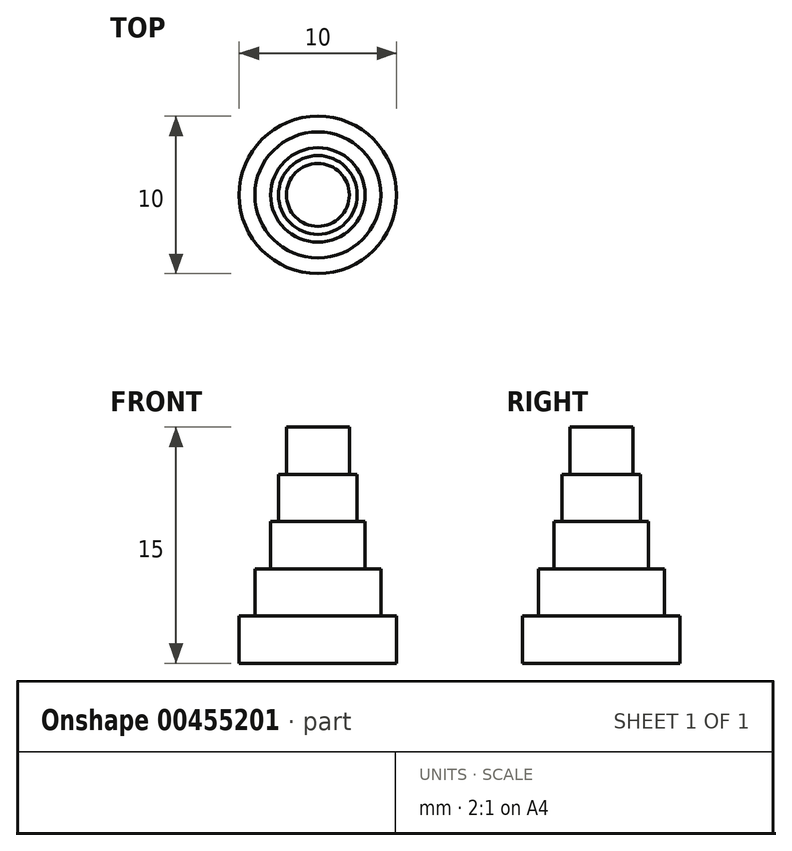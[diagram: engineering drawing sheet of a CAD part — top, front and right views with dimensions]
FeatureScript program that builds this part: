
annotation { "Feature Type Name" : "Feature", "Feature Type Description" : "" }
export const myFeature = defineFeature(function(context is Context, id is Id, definition is map)
    precondition{}
    {
        {
            var Q0;
            Q0=qCreatedBy(makeId("Top.planeOp"),FACE);
            var sketch = newSketch(context, id + "F0", { "sketchPlane" : qUnion([Q0])});
            skCircle(sketch, "E0", {"center": v(0, 0) * mm, "radius": 5 * mm});
            skSolve(sketch);
        }
        {
            var Q0;
            Q0=makeQuery(id+"F0.imprint","IMPRINT",FACE,{"disambiguationData":[TD([[makeQuery(id+"F0.imprint","IMPRINT",EDGE,{"derivedFrom":sQuery(id+"F0.wireOp",EDGE,"E0")}),1.0]])]});
            extrude(context, id + "F1", {"entities" : qUnion([Q0]), "depth" : 3 * mm});
        }
        {
            var Q0;
            Q0=makeQuery(id+"F1.opExtrude","CAP_FACE",FACE,{"disambiguationData":[OSD([sQuery(id+"F0.wireOp",EDGE,"E0")])],"isStart":false});
            var sketch = newSketch(context, id + "F2", { "sketchPlane" : qUnion([Q0])});
            skCircle(sketch, "E1", {"center": v(0, 0) * mm, "radius": 4 * mm});
            skSolve(sketch);
        }
        {
            var Q0;
            Q0=makeQuery(id+"F2.imprint","IMPRINT",FACE,{"disambiguationData":[TD([[makeQuery(id+"F2.imprint","IMPRINT",EDGE,{"derivedFrom":sQuery(id+"F2.wireOp",EDGE,"E1")}),1.0]])]});
            extrude(context, id + "F3", {"entities" : qUnion([Q0]), "operationType" : NewBodyOperationType.ADD, "depth" : 3 * mm});
        }
        {
            var Q0;
            Q0=makeQuery(id+"F3.opExtrude","CAP_FACE",FACE,{"disambiguationData":[OSD([sQuery(id+"F2.wireOp",EDGE,"E1")])],"isStart":false});
            var sketch = newSketch(context, id + "F4", { "sketchPlane" : qUnion([Q0])});
            skCircle(sketch, "E2", {"center": v(0, 0) * mm, "radius": 3 * mm});
            skSolve(sketch);
        }
        {
            var Q0;
            Q0=makeQuery(id+"F4.imprint","IMPRINT",FACE,{"disambiguationData":[TD([[makeQuery(id+"F4.imprint","IMPRINT",EDGE,{"derivedFrom":sQuery(id+"F4.wireOp",EDGE,"E2")}),1.0]])]});
            extrude(context, id + "F5", {"entities" : qUnion([Q0]), "operationType" : NewBodyOperationType.ADD, "depth" : 3 * mm});
        }
        {
            var Q0;
            Q0=makeQuery(id+"F5.opExtrude","CAP_FACE",FACE,{"disambiguationData":[OSD([sQuery(id+"F4.wireOp",EDGE,"E2")])],"isStart":false});
            var sketch = newSketch(context, id + "F6", { "sketchPlane" : qUnion([Q0])});
            skCircle(sketch, "E3", {"center": v(0, 0) * mm, "radius": 2.5 * mm});
            skSolve(sketch);
        }
        {
            var Q0;
            Q0=makeQuery(id+"F6.imprint","IMPRINT",FACE,{"disambiguationData":[TD([[makeQuery(id+"F6.imprint","IMPRINT",EDGE,{"derivedFrom":sQuery(id+"F6.wireOp",EDGE,"E3")}),1.0]])]});
            extrude(context, id + "F7", {"entities" : qUnion([Q0]), "operationType" : NewBodyOperationType.ADD, "depth" : 3 * mm});
        }
        {
            var Q0;
            Q0=makeQuery(id+"F7.opExtrude","CAP_FACE",FACE,{"disambiguationData":[OSD([sQuery(id+"F6.wireOp",EDGE,"E3")])],"isStart":false});
            var sketch = newSketch(context, id + "F8", { "sketchPlane" : qUnion([Q0])});
            skCircle(sketch, "E4", {"center": v(0, 0) * mm, "radius": 2 * mm});
            skSolve(sketch);
        }
        {
            var Q0;
            Q0=makeQuery(id+"F8.imprint","IMPRINT",FACE,{"disambiguationData":[TD([[makeQuery(id+"F8.imprint","IMPRINT",EDGE,{"derivedFrom":sQuery(id+"F8.wireOp",EDGE,"E4")}),1.0]])]});
            extrude(context, id + "F9", {"entities" : qUnion([Q0]), "operationType" : NewBodyOperationType.ADD, "depth" : 3 * mm});
        }
    });
